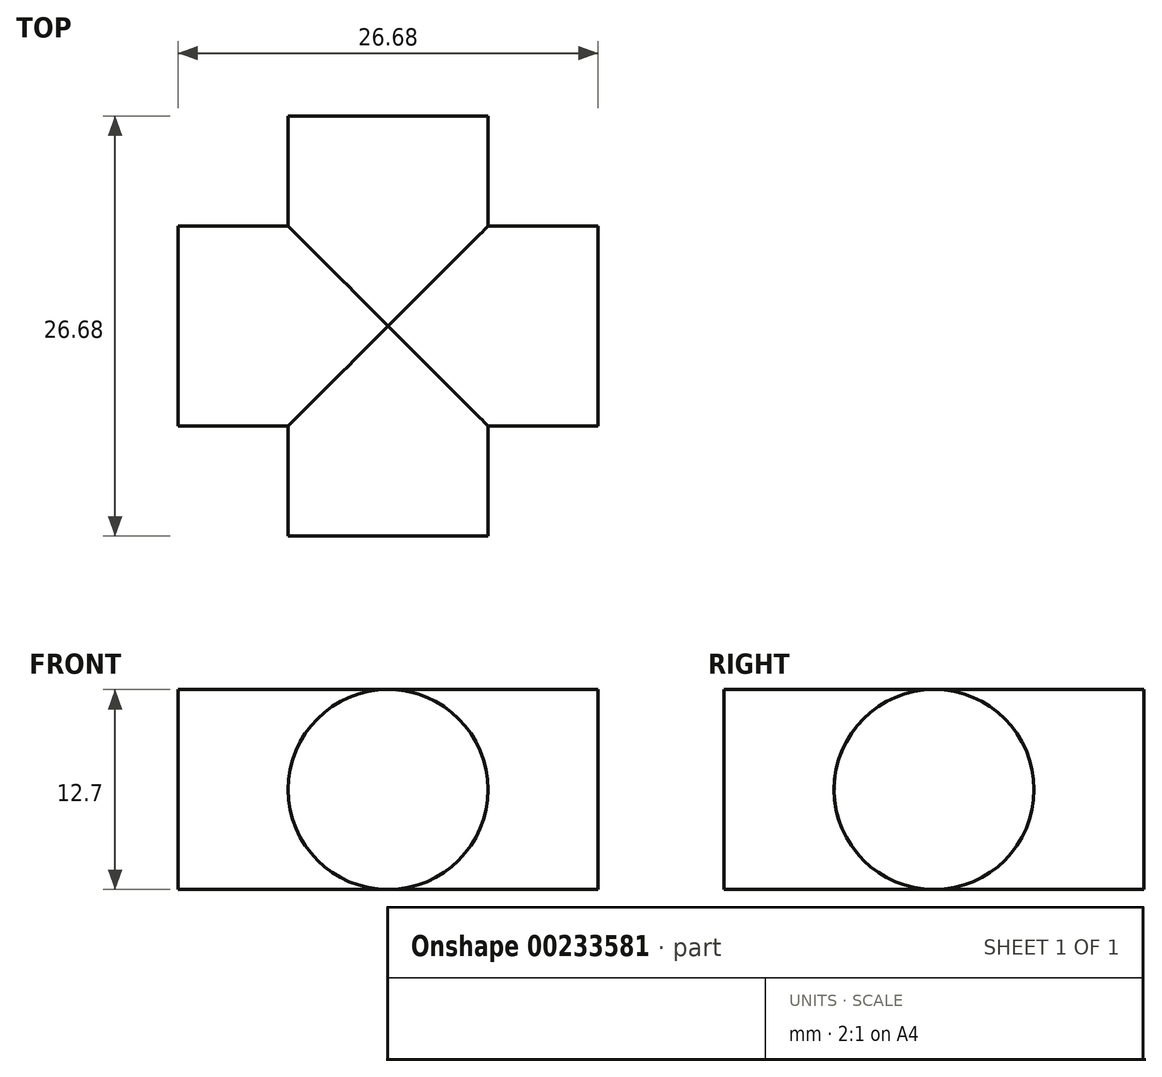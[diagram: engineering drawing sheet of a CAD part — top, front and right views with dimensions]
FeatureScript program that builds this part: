
annotation { "Feature Type Name" : "Feature", "Feature Type Description" : "" }
export const myFeature = defineFeature(function(context is Context, id is Id, definition is map)
    precondition{}
    {
        {
            var Q0;
            Q0=qCreatedBy(makeId("Front.planeOp"),FACE);
            var sketch = newSketch(context, id + "F0", { "sketchPlane" : qUnion([Q0])});
            skCircle(sketch, "E0", {"center": v(0, 0) * mm, "radius": 6.35 * mm});
            skSolve(sketch);
        }
        {
            var Q0;
            Q0=qCreatedBy(makeId("Right.planeOp"),FACE);
            var sketch = newSketch(context, id + "F1", { "sketchPlane" : qUnion([Q0])});
            skCircle(sketch, "E1", {"center": v(0, 0) * mm, "radius": 6.35 * mm});
            skSolve(sketch);
        }
        {
            var Q0;
            Q0=makeQuery(id+"F0.imprint","IMPRINT",FACE,{"disambiguationData":[TD([[makeQuery(id+"F0.imprint","IMPRINT",EDGE,{"derivedFrom":sQuery(id+"F0.wireOp",EDGE,"E0")}),1.0]])]});
            extrude(context, id + "F2", {"entities" : qUnion([Q0]), "endBound" : BoundingType.SYMMETRIC, "depth" : 26.67 * mm});
        }
        {
            var Q0;
            Q0=makeQuery(id+"F1.imprint","IMPRINT",FACE,{"disambiguationData":[TD([[makeQuery(id+"F1.imprint","IMPRINT",EDGE,{"derivedFrom":sQuery(id+"F1.wireOp",EDGE,"E1")}),1.0]])]});
            extrude(context, id + "F3", {"entities" : qUnion([Q0]), "operationType" : NewBodyOperationType.ADD, "endBound" : BoundingType.SYMMETRIC, "depth" : 26.67 * mm});
        }
    });
